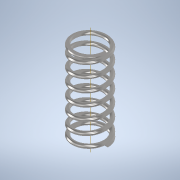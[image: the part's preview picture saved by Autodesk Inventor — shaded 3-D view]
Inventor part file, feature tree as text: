
AUTODESK INVENTOR PART (.ipt)
format: ipt  version: 2020 (Build 240168000, 168)  size: 635,392 bytes
history: native  units: mm
features: extrude x1
ambient origin geometry x8: Origin, YZ Plane, XZ Plane, XY Plane, X Axis, Y Axis, Z Axis, Center Point
bodies: Solid1 (feature_tree)
feature tree (1):
  extrude  "Extrude1"  [1 undecoded]
note: 1 required parameter value undecoded (feature->parameter linkage not recoverable at this tier; creation-order binding heuristic only, values carry confidence <= 0.55)
